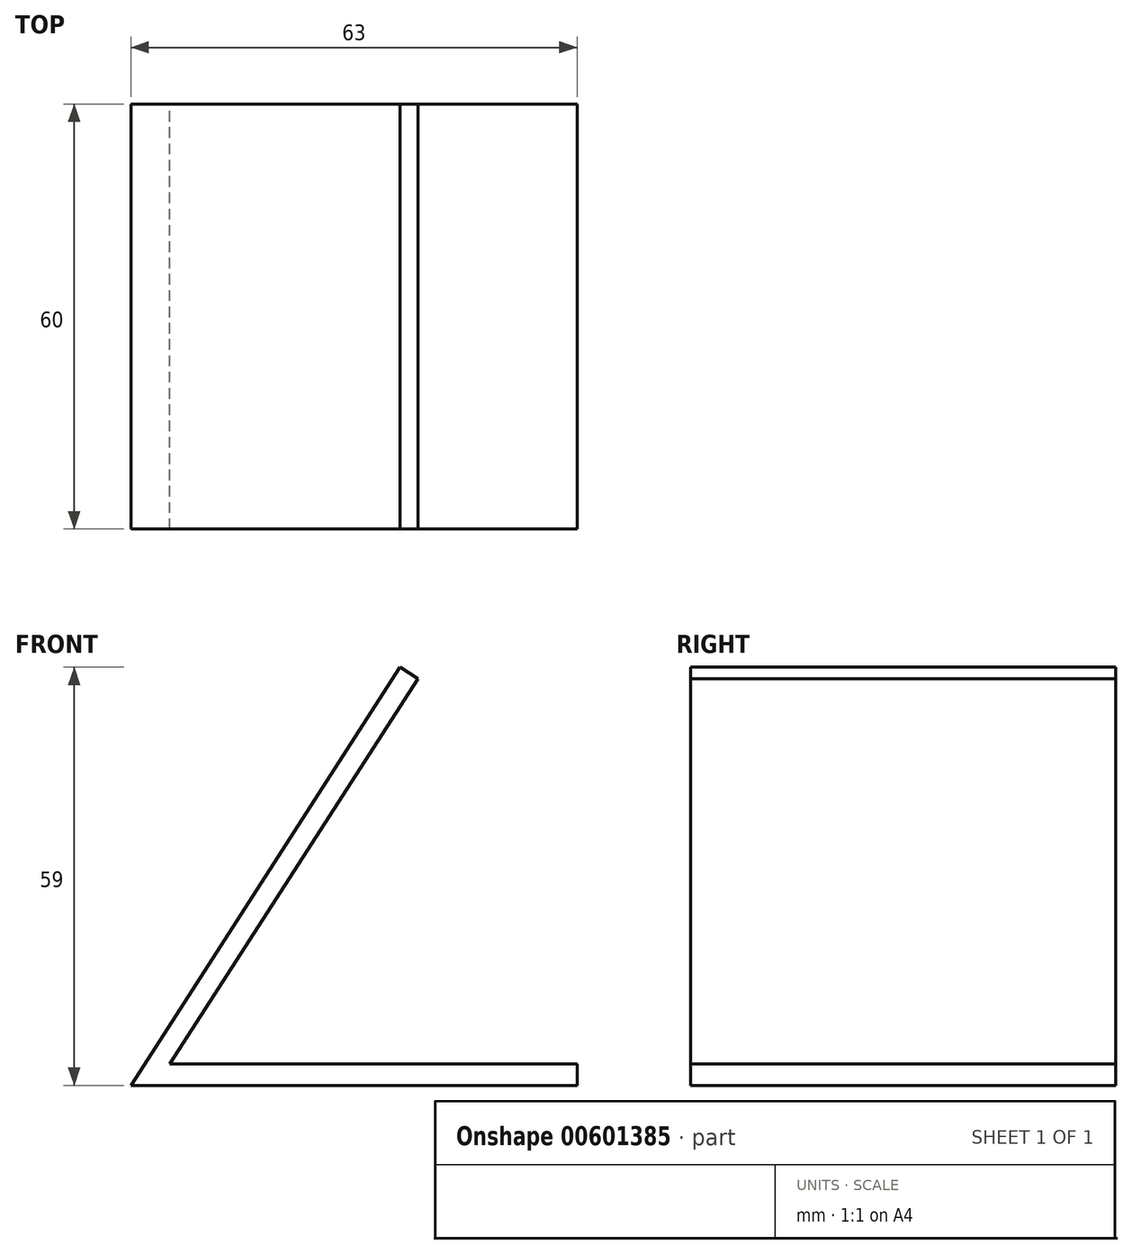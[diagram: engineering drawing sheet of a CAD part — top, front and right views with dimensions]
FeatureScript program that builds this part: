
annotation { "Feature Type Name" : "Feature", "Feature Type Description" : "" }
export const myFeature = defineFeature(function(context is Context, id is Id, definition is map)
    precondition{}
    {
        {
            var Q0;
            Q0=qCreatedBy(makeId("Front.planeOp"),FACE);
            var sketch = newSketch(context, id + "F0", { "sketchPlane" : qUnion([Q0])});
            skLineSegment(sketch, "E0", {"start": v(0, 0) * mm, "end": v(-63, 0) * mm});
            skLineSegment(sketch, "E1", {"start": v(-63, 0) * mm, "end": v(-25, 59) * mm});
            skLineSegment(sketch, "E2", {"start": v(-25, 59) * mm, "end": v(-25, -119.55) * mm, "construction": true});
            skLineSegment(sketch, "E3", {"start": v(-25, 59) * mm, "end": v(-22.48, 57.38) * mm});
            skLineSegment(sketch, "E4", {"start": v(-22.48, 57.38) * mm, "end": v(-57.5, 3) * mm});
            skLineSegment(sketch, "E5", {"start": v(-57.5, 3) * mm, "end": v(0, 3) * mm});
            skLineSegment(sketch, "E6", {"start": v(0, 3) * mm, "end": v(0, 0) * mm});
            skSolve(sketch);
        }
        {
            var Q0;
            Q0 = qSketchRegion(id + "F0", true);
            extrude(context, id + "F1", {"entities" : qUnion([Q0]), "depth" : 60 * mm, "offsetDistance" : 25 * mm});
        }
    });
